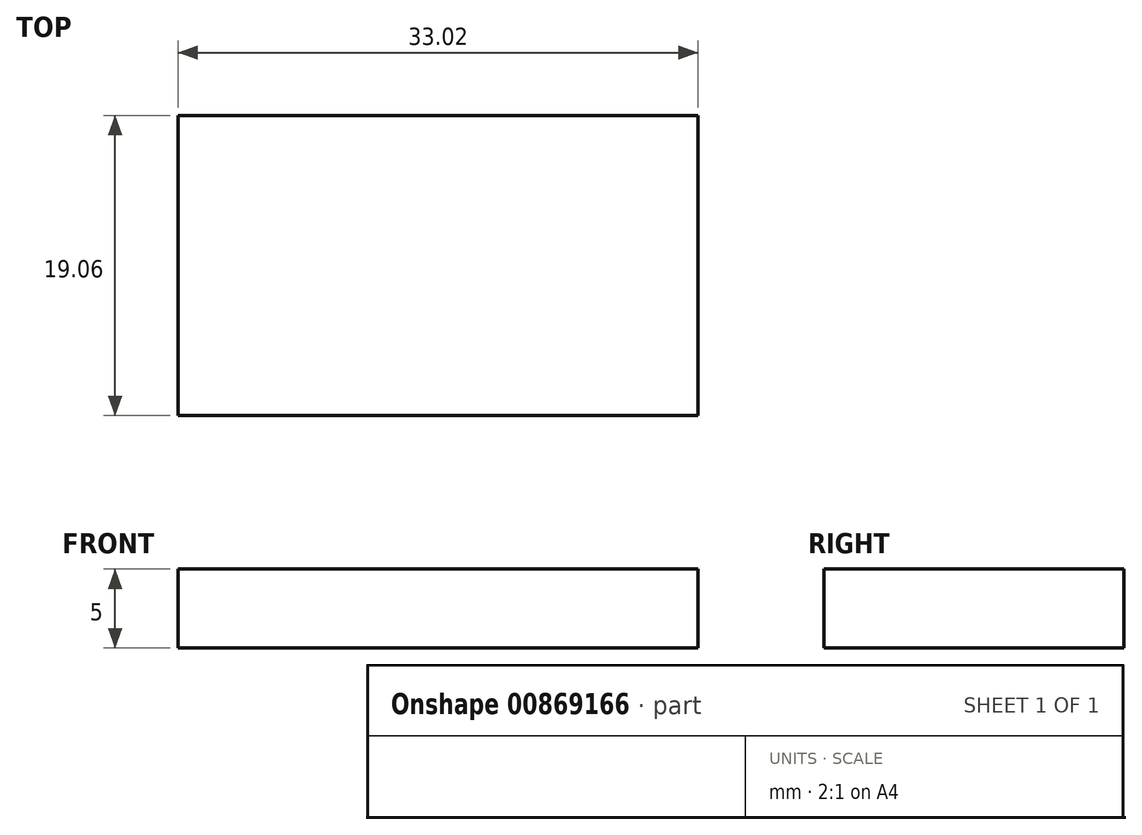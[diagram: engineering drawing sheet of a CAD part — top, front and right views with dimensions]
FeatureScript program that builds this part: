
annotation { "Feature Type Name" : "Feature", "Feature Type Description" : "" }
export const myFeature = defineFeature(function(context is Context, id is Id, definition is map)
    precondition{}
    {
        {
            var Q0;
            Q0=qCreatedBy(makeId("Top.planeOp"),FACE);
            var sketch = newSketch(context, id + "F0", { "sketchPlane" : qUnion([Q0])});
            skLineSegment(sketch, "E0.bottom", {"start": v(-16.51, 9.53) * mm, "end": v(16.51, 9.53) * mm});
            skLineSegment(sketch, "E0.top", {"start": v(-16.51, -9.53) * mm, "end": v(16.51, -9.53) * mm});
            skLineSegment(sketch, "E0.left", {"start": v(-16.51, 9.53) * mm, "end": v(-16.51, -9.53) * mm});
            skLineSegment(sketch, "E0.right", {"start": v(16.51, 9.53) * mm, "end": v(16.51, -9.53) * mm});
            skLineSegment(sketch, "E1", {"start": v(-16.51, 9.53) * mm, "end": v(16.51, -9.52) * mm, "construction": true});
            skSolve(sketch);
        }
        {
            var Q0;
            Q0=qSketchRegion(id+"F0",true);
            extrude(context, id + "F1", {"entities" : qUnion([Q0]), "depth" : 5 * mm, "offsetDistance" : 25 * mm});
        }
    });
